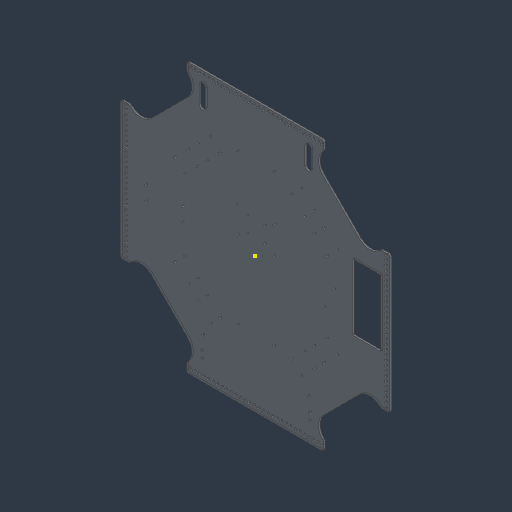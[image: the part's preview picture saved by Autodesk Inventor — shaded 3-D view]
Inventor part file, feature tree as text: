
AUTODESK INVENTOR PART (.ipt)
format: ipt  version: 2024.3 (Build 283343000, 343)  size: 506,880 bytes
history: native  units: mm
features: sketch x12, hole x8, other x6, chamfer x3, pattern_circular x2, sheet_metal_op x1, extrude x1, pattern_linear x1, reference x1
ambient origin geometry x8: Origin, YZ Plane, XZ Plane, XY Plane, X Axis, Y Axis, Z Axis, Center Point
bodies: Body1 (feature_tree)
feature tree (35):
  sketch  "Sketch5"  dims[d22=749.3mm d23=749.3mm]
  sheet_metal_op  "Face1"
  extrude  "Extrusion3"  Depth=749.3mm
  chamfer  "Corner Round1"
  pattern_circular  "Circular Pattern1"  Count=4 Angle=360.0deg
  chamfer  "Corner Round2"
  hole  "Hole1"  [1 undecoded]
  hole  "Hole2"  [1 undecoded]
  pattern_linear  "Rectangular Pattern1"  Count1=30 Spacing1=12.7mm
  pattern_circular  "Circular Pattern2"  Count=4 Angle=360.0deg
  hole  "Main Breaker"  [1 undecoded]
  hole  "PDP"  [1 undecoded]
  hole  "VRM"  [1 undecoded]
  hole  "RoboRIO"  [1 undecoded]
  hole  "Pneumatics Hub"  [1 undecoded]
  chamfer  "Corner Round3"
  hole  "Hole11"  [1 undecoded]
  sketch  "Sketch17"  dims[d63=4.7625mm d64=0.0mm d65=38.1mm d66=50.8mm d69=3.9624mm d70=9.652mm d71=9.779mm d72=6.35mm d73=14.3117mm d74=25.4mm d75=20.594885mm d79=88.9mm d80=38.1mm d81=57.15mm d82=27.94mm d84=3.9624mm d85=9.652mm d86=9.525mm d87=4.826mm d88=14.3117mm d89=4.7625mm d90=20.594885mm d91=101.6mm d92=25.4mm d93=215.9mm d94=3.9624mm d95=9.652mm d96=9.525mm d97=6.35mm d98=14.3117mm d99=25.4mm d100=20.594885mm d101=43.053mm d102=47.752mm d103=63.5mm d104=3.302mm d105=8.3312mm d106=9.525mm d107=6.35mm d108=14.3117mm d109=25.4mm d110=20.594885mm d111=165.1mm d112=101.6mm d113=127.0mm d114=2.9464mm d115=5.6896mm d116=5.5626mm d117=2.8448mm d118=14.3117mm d119=25.4mm d120=20.594885mm d121=101.6mm d122=38.1mm d125=3.9624mm d126=9.652mm d127=9.525mm d128=6.35mm d129=14.3117mm d130=25.4mm d131=20.594885mm d133=78.74mm d134=184.15mm d135=1.5875mm d149=254.0mm d157=17.78mm d158=66.04mm d159=276.225mm d160=279.4mm d161=4.7625mm d162=0.0mm d163=8.89mm d165=349.25mm d166=203.2mm d168=53.975mm d170=25.4mm d178=299.6565mm d179=63.5mm d180=5.1054mm d181=19.05mm d182=9.525mm d183=6.35mm d184=14.3117mm d185=25.4mm d186=20.594885mm d187=19.05mm d188=8.7376mm d189=38.1mm d190=8.7376mm d191=38.1mm]
  other  "Plate1"
  sketch  "Sketch6"  dims[d24=184.15mm]
  sketch  "Sketch7"  dims[d27=25.4mm]
  sketch  "Sketch8"  dims[d29=40.165946mm]
  sketch  "Sketch9"  dims[d31=158.75mm]
  sketch  "Sketch10"  dims[d32=4.7625mm]
  sketch  "Sketch11"  dims[d33=0.0mm d34=0.0mm d35=40.0mm d36=360.0deg]
  sketch  "Sketch12"  dims[d38=6.35mm d39=6.0mm]
  sketch  "Sketch13"  dims[d40=6.35mm d41=12.7mm]
  sketch  "Sketch15"  dims[d42=5.1054mm d43=19.05mm d44=9.779mm d45=6.35mm d46=14.3117mm d47=4.7625mm]
  sketch  "Sketch16"  dims[d48=20.594885mm d49=300.0mm d51=12.7mm d52=40.0mm d53=360.0deg]
  reference  "Reference21"
  other  "Cut1"
  other  "Cut2"
  other  "<userpath>\Documents\GitHub\2025-Poseidon-Mechanical\#Poseidon 2025.iam"
  other  "#Poseidon 2025.iam"
  other  "ANGLE,MOUNT,ELEVATOR,MIRR.ipt:1"
note: 8 required parameter values undecoded (feature->parameter linkage not recoverable at this tier; creation-order binding heuristic only, values carry confidence <= 0.55)
